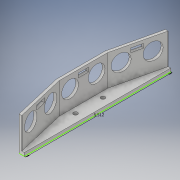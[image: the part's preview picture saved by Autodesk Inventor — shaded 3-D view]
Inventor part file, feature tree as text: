
AUTODESK INVENTOR PART (.ipt)
format: ipt  version: 2019 (Build 230136000, 136)  size: 193,024 bytes
history: native  units: in
note: dims shown in document units (in); Inventor stores cm internally (conversion verified against a paired STEP export)
features: extrude x5, sketch x5, hole x4, imported_body x1, other x1
ambient origin geometry x8: Origin, YZ Plane, XZ Plane, XY Plane, X Axis, Y Axis, Z Axis, Center Point
bodies: Solid1 (feature_tree)
feature tree (16):
  imported_body  "Base"
  extrude  "Extrusion1"  Depth=0.1181in TaperAngle=0.0deg
  extrude  "Extrusion2"  Depth=1.16in TaperAngle=0.0deg
  sketch  "Sketch3"  dims[d1=5.5118in d4=0.1181in d5=0.0in]
  hole  "Hole1"  [1 undecoded]
  extrude  "Extrusion3"  Depth=1.16in TaperAngle=0.0deg
  sketch  "Sketch4"  dims[d6=0.1in d7=1.16in d8=0.0in]
  sketch  "Sketch5"  dims[d9=1.887in d10=1.7894in]
  hole  "Hole2"  [1 undecoded]
  extrude  "Extrusion4"  Depth=1.16in TaperAngle=0.0deg
  sketch  "Sketch6"  dims[d11=0.8071in]
  hole  "Hole3"  [1 undecoded]
  extrude  "Extrusion5"  [1 undecoded]
  hole  "Hole4"  [1 undecoded]
  other  "FrontWall"
  sketch  "Sketch7"  dims[d18=0.6299in d19=0.75in d20=0.375in d21=0.25in d22=0.5635in d23=1.0in d24=0.8108in d25=1.16in d26=0.0in d27=1.887in d28=1.7894in d29=0.8071in d30=0.6299in d31=0.75in d32=0.375in d33=0.25in d34=0.5635in d35=1.0in d36=0.8108in d37=1.16in d38=0.0in d39=0.031in d40=1.7894in d41=0.8071in d42=0.6299in d43=0.75in d44=0.375in d45=0.25in d46=0.5635in d47=1.0in d48=0.8108in d49=1.16in d50=0.0in d53=0.1575in d54=0.75in d55=0.375in d56=0.25in d57=0.5635in d58=1.0in d59=0.8108in]
note: 5 required parameter values undecoded (feature->parameter linkage not recoverable at this tier; creation-order binding heuristic only, values carry confidence <= 0.55)
